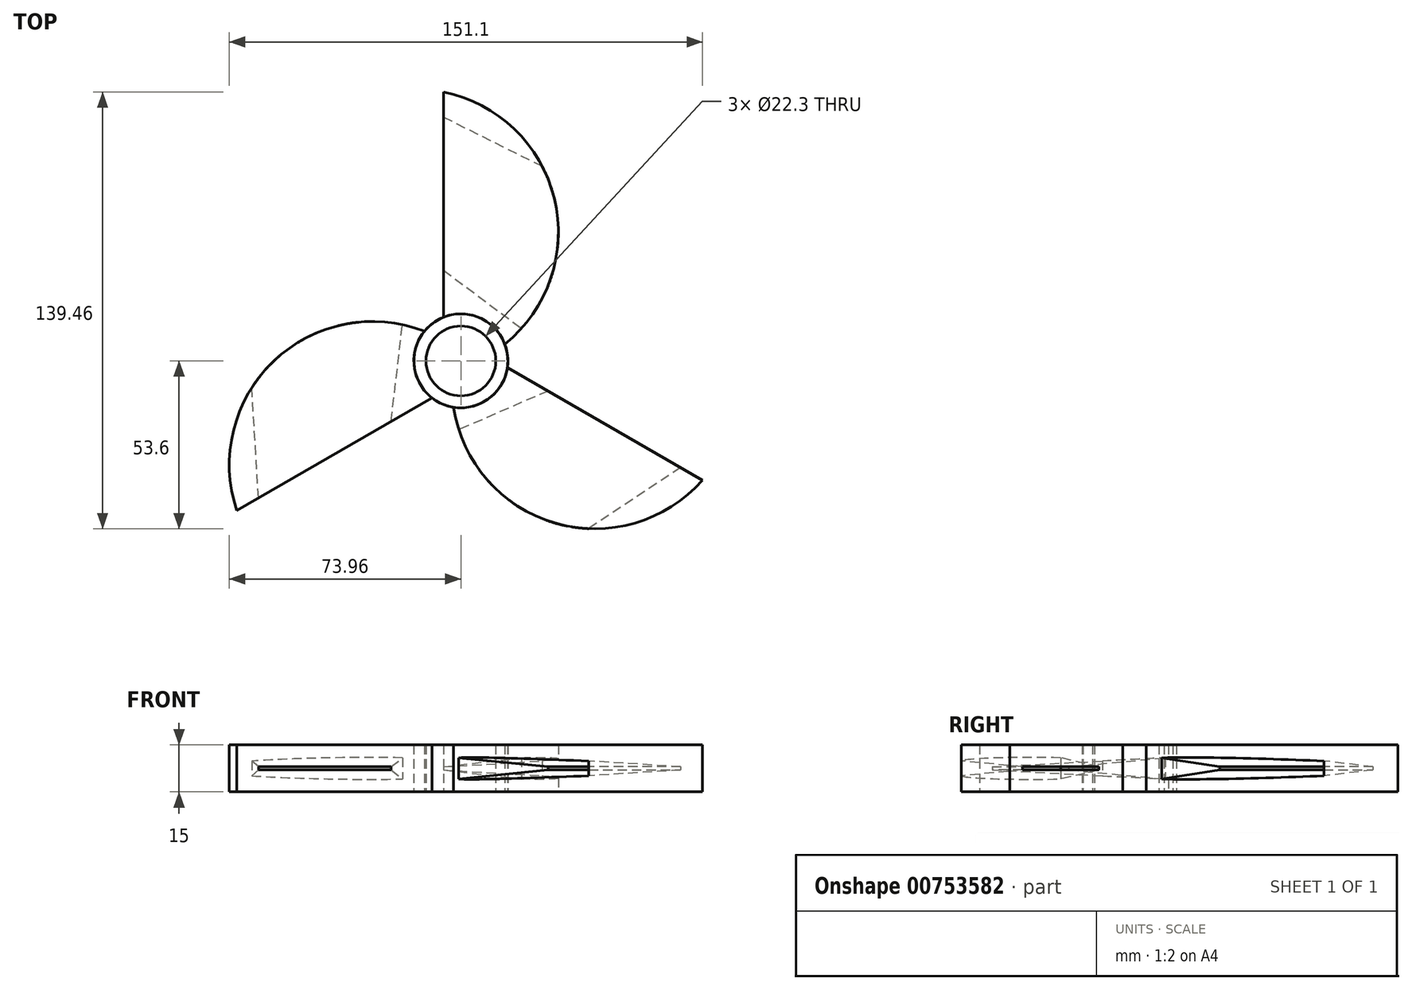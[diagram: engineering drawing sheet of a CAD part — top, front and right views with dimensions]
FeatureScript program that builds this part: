
annotation { "Feature Type Name" : "Feature", "Feature Type Description" : "" }
export const myFeature = defineFeature(function(context is Context, id is Id, definition is map)
    precondition{}
    {
        {
            var Q0;
            Q0=qCreatedBy(makeId("Top.planeOp"),FACE);
            var sketch = newSketch(context, id + "F0", { "sketchPlane" : qUnion([Q0])});
            skCircle(sketch, "E0", {"center": v(0, 0) * mm, "radius": 11.15 * mm});
            skPoint(sketch, "E1", {"position": v(-5.58, 0) * mm});
            skPoint(sketch, "E2.MirrorP", {"position": v(5.58, 0) * mm});
            skLineSegment(sketch, "E3.1.0", {"start": v(-5.57, -9.66) * mm, "end": v(-71.57, -47.76) * mm});
            skArc(sketch, "E4.1.0", {"start": v(-2.79, 4.83) * mm, "mid": v(-56, 3.17) * mm, "end": v(-71.57, -47.76) * mm});
            skCircle(sketch, "E5", {"center": v(0, 0) * mm, "radius": 15 * mm});
            skSolve(sketch);
        }
        {
            var Q0;
            {var subQ0=sQuery(id+"F0.wireOp",EDGE,"qT4FRHWR-IBJN-9FKa-ra2Q-R30YMDbe0SES");Q0=makeQuery(id+"F0.imprint","IMPRINT",FACE,{"disambiguationData":[TD([[makeQuery(id+"F0.imprint","IMPRINT",EDGE,{"derivedFrom":subQ0}),-1.0]])]});}
            var Q1;
            {var subQ0=sQuery(id+"F0.wireOp",EDGE,"E3.2.0");Q1=makeQuery(id+"F0.imprint","IMPRINT",FACE,{"disambiguationData":[TD([[makeQuery(id+"F0.imprint","IMPRINT",EDGE,{"derivedFrom":subQ0}),-1.0]])]});}
            var Q2;
            {var subQ0=sQuery(id+"F0.wireOp",EDGE,"E3.1.0");Q2=makeQuery(id+"F0.imprint","IMPRINT",FACE,{"disambiguationData":[TD([[makeQuery(id+"F0.imprint","IMPRINT",EDGE,{"derivedFrom":subQ0}),-1.0]])]});}
            var Q3;
            {var subQ0=sQuery(id+"F0.wireOp",EDGE,"E3.2.0");var subQ1=sQuery(id+"F0.wireOp",EDGE,"E0");var subQ2=makeQuery(id+"F0.imprint","INTERSECT",VERTEX,{"derivedFrom":[subQ1,subQ0]});Q3=makeQuery(id+"F0.imprint","IMPRINT",FACE,{"disambiguationData":[TD([[makeQuery(id+"F0.imprint","IMPRINT",EDGE,{"disambiguationData":[TD([[subQ2,-1.0]])],"derivedFrom":subQ1}),-1.0]])]});}
            var Q4;
            {var subQ0=sQuery(id+"F0.wireOp",EDGE,"E3.2.0");var subQ1=sQuery(id+"F0.wireOp",EDGE,"E0");var subQ2=makeQuery(id+"F0.imprint","INTERSECT",VERTEX,{"derivedFrom":[subQ1,subQ0]});Q4=makeQuery(id+"F0.imprint","IMPRINT",FACE,{"disambiguationData":[TD([[makeQuery(id+"F0.imprint","IMPRINT",EDGE,{"disambiguationData":[TD([[subQ2,1.0]])],"derivedFrom":subQ1}),-1.0]])]});}
            var Q5;
            {var subQ0=sQuery(id+"F0.wireOp",EDGE,"E3.1.0");var subQ1=sQuery(id+"F0.wireOp",EDGE,"E0");var subQ2=makeQuery(id+"F0.imprint","INTERSECT",VERTEX,{"derivedFrom":[subQ1,subQ0]});Q5=makeQuery(id+"F0.imprint","IMPRINT",FACE,{"disambiguationData":[TD([[makeQuery(id+"F0.imprint","IMPRINT",EDGE,{"disambiguationData":[TD([[subQ2,-1.0]])],"derivedFrom":subQ1}),-1.0]])]});}
            var Q6;
            {var subQ0=sQuery(id+"F0.wireOp",EDGE,"qT4FRHWR-IBJN-9FKa-ra2Q-R30YMDbe0SES");var subQ1=sQuery(id+"F0.wireOp",EDGE,"E0");var subQ2=makeQuery(id+"F0.imprint","INTERSECT",VERTEX,{"derivedFrom":[subQ1,subQ0]});Q6=makeQuery(id+"F0.imprint","IMPRINT",FACE,{"disambiguationData":[TD([[makeQuery(id+"F0.imprint","IMPRINT",EDGE,{"disambiguationData":[TD([[subQ2,-1.0]])],"derivedFrom":subQ1}),-1.0]])]});}
            var Q7;
            {var subQ0=sQuery(id+"F0.wireOp",EDGE,"qT4FRHWR-IBJN-9FKa-ra2Q-R30YMDbe0SES");var subQ1=sQuery(id+"F0.wireOp",EDGE,"E0");var subQ2=makeQuery(id+"F0.imprint","INTERSECT",VERTEX,{"derivedFrom":[subQ1,subQ0]});Q7=makeQuery(id+"F0.imprint","IMPRINT",FACE,{"disambiguationData":[TD([[makeQuery(id+"F0.imprint","IMPRINT",EDGE,{"disambiguationData":[TD([[subQ2,1.0]])],"derivedFrom":subQ1}),-1.0]])]});}
            var Q8;
            {var subQ0=sQuery(id+"F0.wireOp",EDGE,"E3.1.0");var subQ1=sQuery(id+"F0.wireOp",EDGE,"E0");var subQ2=makeQuery(id+"F0.imprint","INTERSECT",VERTEX,{"derivedFrom":[subQ1,subQ0]});Q8=makeQuery(id+"F0.imprint","IMPRINT",FACE,{"disambiguationData":[TD([[makeQuery(id+"F0.imprint","IMPRINT",EDGE,{"disambiguationData":[TD([[subQ2,1.0]])],"derivedFrom":subQ1}),-1.0]])]});}
            extrude(context, id + "F1", {"entities" : qUnion([Q0, Q1, Q2, Q3, Q4, Q5, Q6, Q7, Q8]), "depth" : 15 * mm, "offsetDistance" : 25.4 * mm});
        }
        {
            var Q0;
            Q0=makeQuery(id+"F1.opExtrude","SWEPT_FACE",FACE,{"disambiguationData":[OSD([sQuery(id+"F0.wireOp",EDGE,"E3.1.0")])]});
            var sketch = newSketch(context, id + "F2", { "sketchPlane" : qUnion([Q0])});
            skLineSegment(sketch, "E6.0", {"start": v(-81.86, 11) * mm, "end": v(-17.93, 11) * mm});
            skLineSegment(sketch, "E6.1", {"start": v(-81.86, 4) * mm, "end": v(-81.86, 11) * mm});
            skLineSegment(sketch, "E6.2", {"start": v(-81.86, 4) * mm, "end": v(-17.93, 4) * mm});
            skLineSegment(sketch, "E7.MirrorCS", {"start": v(101.17, 11) * mm, "end": v(37.24, 11) * mm});
            skLineSegment(sketch, "E8.MirrorCS", {"start": v(101.17, 4) * mm, "end": v(101.17, 11) * mm});
            skLineSegment(sketch, "E9.MirrorCS", {"start": v(101.17, 4) * mm, "end": v(37.24, 4) * mm});
            skLineSegment(sketch, "E10.MirrorCS", {"start": v(37.24, 4) * mm, "end": v(37.24, 11) * mm});
            skLineSegment(sketch, "E11", {"start": v(-24.62, 11) * mm, "end": v(-24.62, 4) * mm});
            skLineSegment(sketch, "E12.0", {"start": v(-77.86, 8) * mm, "end": v(-21.93, 8) * mm});
            skLineSegment(sketch, "E12.1", {"start": v(-77.86, 8) * mm, "end": v(-77.86, 7) * mm});
            skLineSegment(sketch, "E12.2", {"start": v(-21.93, 7) * mm, "end": v(-77.86, 7) * mm});
            skLineSegment(sketch, "E13", {"start": v(-28.94, 8) * mm, "end": v(-28.94, 7) * mm});
            skSolve(sketch);
        }
        {
            var Q0;
            Q0=qCreatedBy(makeId("Front.planeOp"),FACE);
            cPlane(context, id + "F3", {"entities" : qUnion([Q0]), "cplaneType" : CPlaneType.OFFSET, "offset" : 12.7 * mm, "oppositeDirection" : true, "width" : 152.4 * mm, "height" : 152.4 * mm});
        }
        {
            var Q0;
            Q0=qCreatedBy(makeId("Front.planeOp"),FACE);
            var sketch = newSketch(context, id + "F4", { "sketchPlane" : qUnion([Q0])});
            skLineSegment(sketch, "E14", {"start": v(0, 71.34) * mm, "end": v(0, -51.88) * mm, "construction": true});
            skSolve(sketch);
        }
        {
            var Q0;
            Q0=qCreatedBy(id+"F3.planeOp",FACE);
            var sketch = newSketch(context, id + "F5", { "sketchPlane" : qUnion([Q0])});
            skPoint(sketch, "E15", {"position": v(-4.17, 11) * mm});
            skPoint(sketch, "E16", {"position": v(-68.1, 4) * mm});
            skLineSegment(sketch, "E17.bottom", {"start": v(-4.17, 11) * mm, "end": v(-68.1, 11) * mm});
            skLineSegment(sketch, "E17.top", {"start": v(-4.17, 4) * mm, "end": v(-68.1, 4) * mm});
            skLineSegment(sketch, "E17.right", {"start": v(-68.1, 11) * mm, "end": v(-68.1, 4) * mm});
            skLineSegment(sketch, "E18", {"start": v(-18.54, 11) * mm, "end": v(-18.54, 4) * mm});
            skSolve(sketch);
        }
        {
            var Q1;
            {var subQ0=sQuery(id+"F2.wireOp",EDGE,"E12.1");Q1=makeQuery(id+"F2.imprint","IMPRINT",FACE,{"disambiguationData":[TD([[makeQuery(id+"F2.imprint","IMPRINT",EDGE,{"derivedFrom":subQ0}),1.0]])]});}
            var Q2;
            {var subQ0=sQuery(id+"F5.wireOp",EDGE,"E17.right");Q2=makeQuery(id+"F5.imprint","IMPRINT",FACE,{"disambiguationData":[TD([[makeQuery(id+"F5.imprint","IMPRINT",EDGE,{"derivedFrom":subQ0}),1.0]])]});}
            loft(context, id + "F6", {"operationType" : NewBodyOperationType.REMOVE, "sheetProfilesArray" : [{ "sheetProfileEntities" : qUnion([Q1]) }, { "sheetProfileEntities" : qUnion([Q2]) }]});
        }
        {
            var Q0;
            Q0=makeQuery(id+"F1.opExtrude","SWEPT_BODY",BODY,{"disambiguationData":[OSD([sQuery(id+"F0.wireOp",EDGE,"E0"),sQuery(id+"F0.wireOp",EDGE,"E3.1.0"),sQuery(id+"F0.wireOp",EDGE,"E4.1.0"),sQuery(id+"F0.wireOp",EDGE,"E5")])]});
            var Q1;
            Q1=sQuery(id+"F4.wireOp",EDGE,"E14");
            circularPattern(context, id + "F7", {"entities" : qUnion([Q0]), "axis" : qUnion([Q1]), "angle" : 360 * degree, "instanceCount" : 3, "equalSpace" : true});
        }
    });
